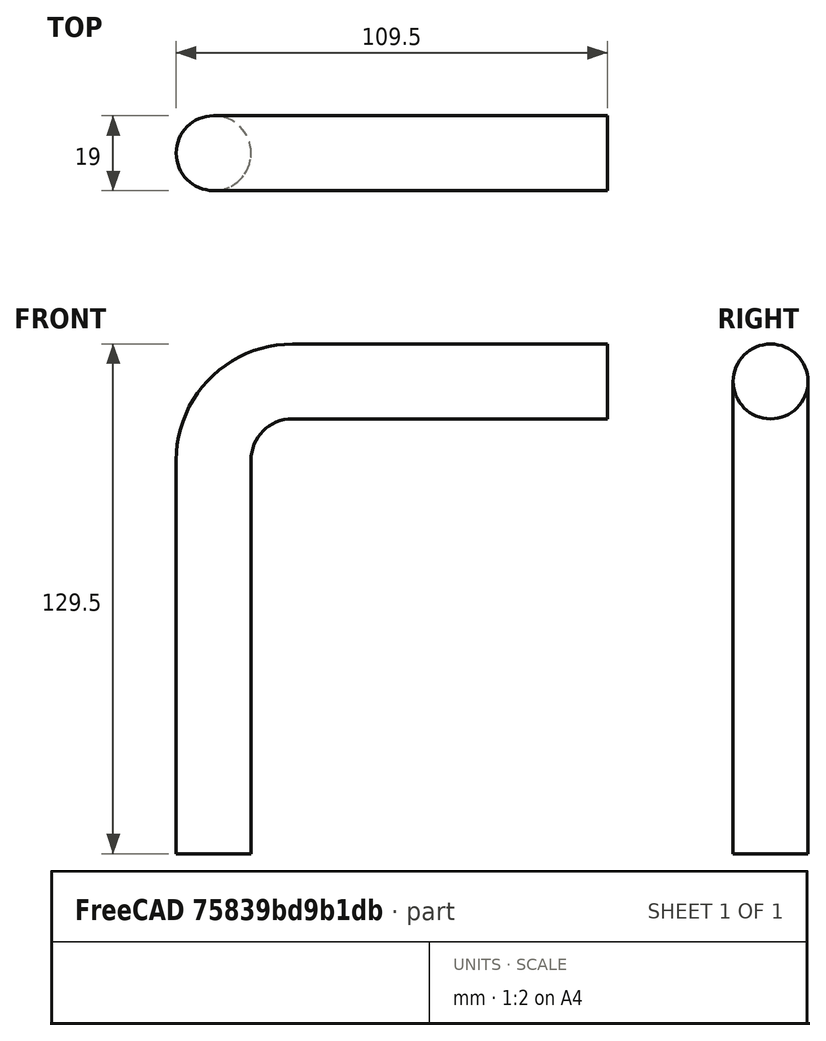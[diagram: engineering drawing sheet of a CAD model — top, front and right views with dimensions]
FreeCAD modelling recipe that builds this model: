
FCSTD DOCUMENT  (FreeCAD 0.17R10990 (Git))
Label: guide pin
License: All rights reserved
LicenseURL: http://en.wikipedia.org/wiki/All_rights_reserved
objects: Sketcher::SketchObject×2, Spreadsheet::Sheet×1, PartDesign::AdditivePipe×1, PartDesign::Body×1
note: 5 computed .brp shape members not serialized (recipe doc carries the construction recipe); baked Part::Feature solids carry a one-line shape summary decoded from their .brp

FEATURE [Spreadsheet::Sheet] Spreadsheet  label="DImensions"
  cells = A1=base frame cross section; B1(baseframecrosssection)==50mm; A2=thickness; B2(thickness)==10mm; A3=inside thickness; B3(insidethickness)==B1 - 2 * B2; A4=base frame length; B4(baseframelength)==1100mm; A5=turn angle; B5(turnangle)==90deg; A6=distance of base frame support rod from origin; B6(distanceofbaseframesupportrodfromorigin)==200mm; A7=base frame support rod length; B7(baseframesupportrodlength)==1200mm; A8=distance between second base frame support rod; B8(distancebetweensecondbaseframesupportrod)==B4 - B6; A9=distance of vertical rods from origin; B9(distanceofverticalrodsfromorigin)==B16 * 0.5; A10=radius stopper rod pocket; B10(radiusstopperrodpocket)==20mm; A11=radius stopper rod; B11(radiusstopperrod)==B10 - 0.5mm; A12=half of base frame cross section; B12(halfofbaseframecrosssection)==B1 / 2; A13=base frame width; B13(baseframewidth)==1300mm; A14=half of base frame width; B14(halfofbaseframewidth)==B13 / 2; A15=stopper rod pocket depth; B15(stopperrodpocketdepth)==45mm; A16=length of collector frame; B16(lengthofcollectorframe)==2100mm; A17=height of stopper rod; B17(heightofstopperrod)==1850mm; A18=inner radius stopper rod; B18(innerradiusstopperrod)==B11 - B2; A19=height of hole at 30; B19(heightofholeat30)==606.93600000000004mm; A20=height of hole at 45; B20(heightofholeat45)==1050mm; A21=height of hole at 60; B21(heightofholeat60)==1816.5mm; A22=radius support rod horizontol pocket; B22(radiussupportrodhorizontolpocket)==10mm; A23=radius support rod horizontol; B23(radiussupportrodhorizontol)==B22 - 0.5mm; A24=collector frame length; B24(collectorframelength)==2100mm; A25=collector frame width; B25(collectorframewidth)==1100mm; A26=collector frame height; B26(collectorframeheight)==100mm; A27=collector frame pocket depth; B27(collectorframepocketdepth)==B26 - B2; A28=collector frame width after cut; B28(collectorframewidthaftercut)==150mm; A29=collector frame pocket inner width; B29(collectorframepocketinnerwidth)==B28 - B2; A30=collector frame plane offset; B30(collectorframeplaneoffset)==-B1 / 2; A31=collector frame x distance from origin; B31(collectorframexdistancefromorigin)==(B13 - B25 - B1) / 2; A32=collector frame pocket width; B32(collectorframepocketwidth)==B25 - B2; A33=collector frame pocket length; B33(collectorframepocketlength)==B24 - B2; A34=distance of second vertical rod from origin; B34(distanceofsecondverticalrodfromorigin)==B13 - B12; A35=support pin pocket radius; B35(supportpinpocketradius)==10mm; A36=support pin pocket distance from origin; B36(supportpinpocketdistancefromorigin)==50mm; A37=support pin radius; B37(supportpinradius)==9.5mm; A38=support pin length; B38(supportpinlength)==100mm; A39=support pin height; B39(supportpinheight)==120mm
FEATURE [Sketcher::SketchObject] Sketch
  MapMode = 5
  Support = -> [XY_Plane]
  expr: Constraints[1] = Spreadsheet.supportpinradius
  sketch-geometry (1):
    g0: Circle CenterX=0 CenterY=0 CenterZ=0 NormalX=0 NormalY=0 NormalZ=1 Radius=9.5
  constraints (2):
    c: Coincident(g0,g-1)
    c: Radius(g0) = 9.5
FEATURE [Sketcher::SketchObject] Sketch001
  MapMode = 5
  Placement = pos=(0,0,0) rot=(1,0,0;1.5708rad)
  Support = -> [XZ_Plane]
  expr: Constraints[7] = Spreadsheet.supportpinlength
  expr: Constraints[6] = Spreadsheet.supportpinheight
  sketch-geometry (3):
    g0: LineSegment StartX=0 StartY=0 StartZ=0 EndX=0 EndY=100 EndZ=0
    g1: LineSegment StartX=20 StartY=120 StartZ=0 EndX=100 EndY=120 EndZ=0
    g2: ArcOfCircle CenterX=20 CenterY=100 CenterZ=0 NormalX=0 NormalY=0 NormalZ=1 Radius=20 StartAngle=1.5708 EndAngle=3.14159
  constraints (8):
    c: Coincident(g-1,g0)
    c: Vertical(g0)
    c: Horizontal(g1)
    c: Tangent(g0,g2) = 1.5708
    c: Tangent(g1,g2) = 1.5708
    c: Radius(g2) = 20
    c: DistanceY(g-1,g1) = 120
    c: DistanceX(g-1,g1) = 100
FEATURE [PartDesign::AdditivePipe] AdditivePipe
  AuxilleryCurvelinear = true
  AuxillerySpineTangent = false
  Binormal = (0,0,0)
  Mode = 0
  Profile = -> Sketch
  Spine = -> Sketch001
  SpineTangent = false
  Transformation = 0
  Transition = 2
FEATURE [PartDesign::Body] Body
  Group = -> [Sketch,Sketch001,AdditivePipe]
  Origin = -> BodyOrigin
  Tip = -> AdditivePipe
